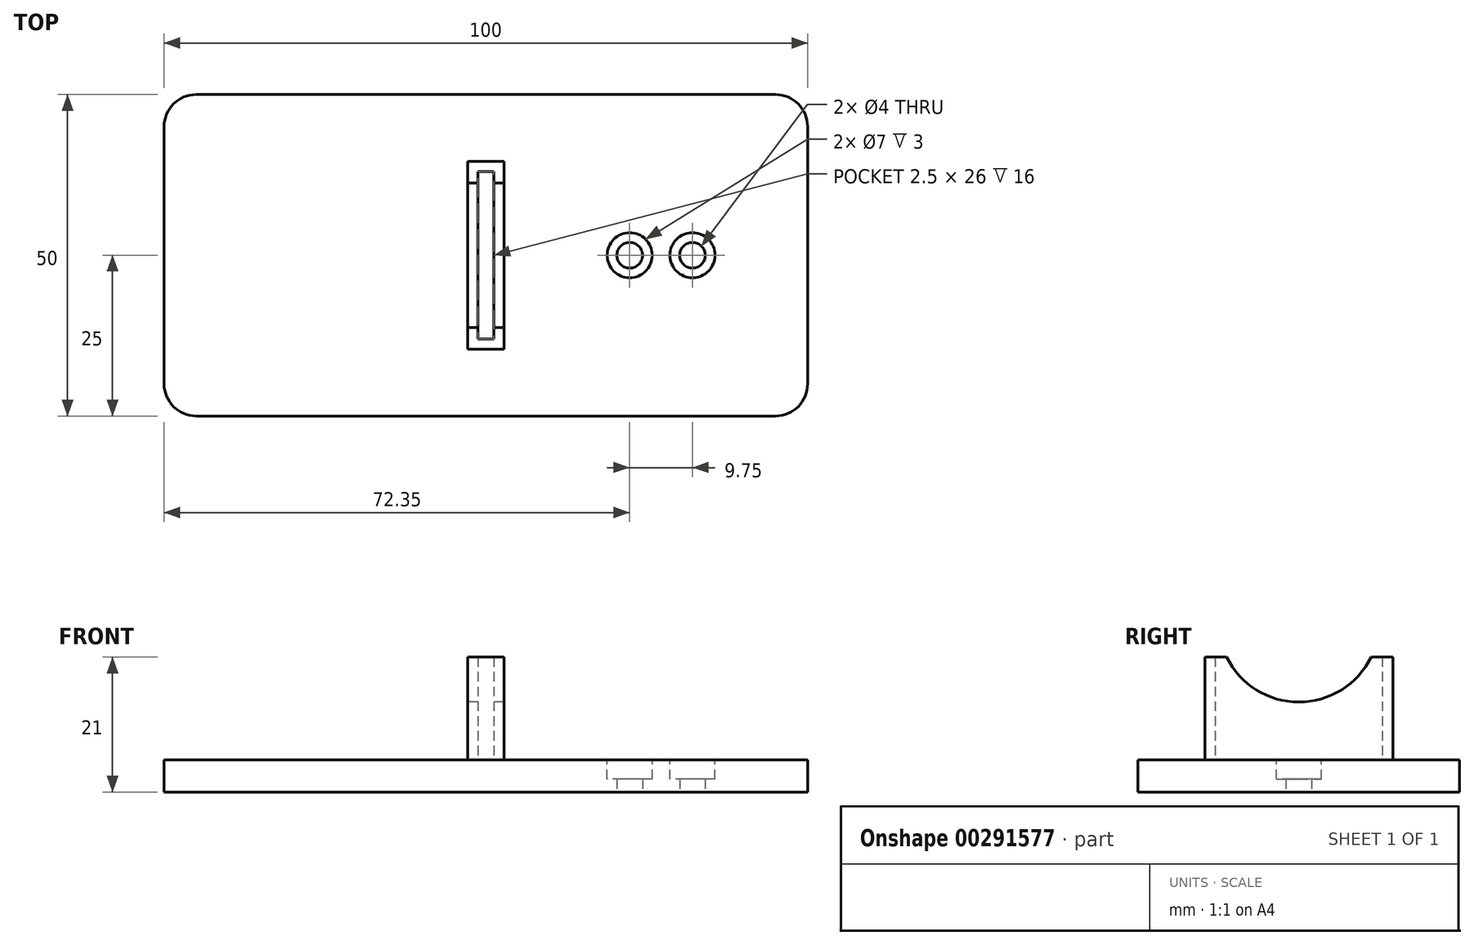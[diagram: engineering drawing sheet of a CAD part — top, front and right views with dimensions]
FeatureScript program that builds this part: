
annotation { "Feature Type Name" : "Feature", "Feature Type Description" : "" }
export const myFeature = defineFeature(function(context is Context, id is Id, definition is map)
    precondition{}
    {
        {
            var Q0;
            Q0=qCreatedBy(makeId("Top.planeOp"),FACE);
            var sketch = newSketch(context, id + "F0", { "sketchPlane" : qUnion([Q0])});
            skLineSegment(sketch, "E0.bottom", {"start": v(50, -25) * mm, "end": v(-50, -25) * mm});
            skLineSegment(sketch, "E0.top", {"start": v(50, 25) * mm, "end": v(-50, 25) * mm});
            skLineSegment(sketch, "E0.left", {"start": v(50, -25) * mm, "end": v(50, 25) * mm});
            skLineSegment(sketch, "E0.right", {"start": v(-50, -25) * mm, "end": v(-50, 25) * mm});
            skPoint(sketch, "E0.middle", {"position": v(0, 0) * mm});
            skLineSegment(sketch, "E1", {"start": v(37.6, 49.23) * mm, "end": v(37.6, -49.65) * mm, "construction": true});
            skLineSegment(sketch, "E2", {"start": v(-37.6, -45.19) * mm, "end": v(-37.6, 49.82) * mm, "construction": true});
            skCircle(sketch, "E3", {"center": v(32.1, 0) * mm, "radius": 2 * mm});
            skCircle(sketch, "E4", {"center": v(22.35, 0) * mm, "radius": 2 * mm});
            skSolve(sketch);
        }
        {
            var Q0;
            Q0=qSketchRegion(id+"F0",true);
            extrude(context, id + "F1", {"entities" : qUnion([Q0]), "depth" : 5 * mm});
        }
        {
            var Q0;
            Q0=makeQuery(id+"F1.opExtrude","CAP_FACE",FACE,{"disambiguationData":[OSD([sQuery(id+"F0.wireOp",EDGE,"E0.bottom"),sQuery(id+"F0.wireOp",EDGE,"E0.top"),sQuery(id+"F0.wireOp",EDGE,"E0.left"),sQuery(id+"F0.wireOp",EDGE,"E0.right"),sQuery(id+"F0.wireOp",EDGE,"E3"),sQuery(id+"F0.wireOp",EDGE,"E4"),sQuery(id+"F0.wireOp",EDGE,"47204b9b-54a0-4112-ab0c-eb390dbab72c0.MirrorC"),sQuery(id+"F0.wireOp",EDGE,"47204b9b-54a0-4112-ab0c-eb390dbab72c1.MirrorC")])],"isStart":false});
            var sketch = newSketch(context, id + "F2", { "sketchPlane" : qUnion([Q0])});
            skCircle(sketch, "E5.0", {"center": v(32.1, 0) * mm, "radius": 2 * mm, "construction": true});
            skCircle(sketch, "E6.0", {"center": v(22.35, 0) * mm, "radius": 2 * mm, "construction": true});
            skCircle(sketch, "E7", {"center": v(32.1, 0) * mm, "radius": 3.5 * mm});
            skCircle(sketch, "E8", {"center": v(22.35, 0) * mm, "radius": 3.5 * mm});
            skSolve(sketch);
        }
        {
            var Q0;
            Q0=qSketchRegion(id+"F2",true);
            extrude(context, id + "F3", {"entities" : qUnion([Q0]), "operationType" : NewBodyOperationType.REMOVE, "oppositeDirection" : true, "depth" : 3 * mm});
        }
        {
            var Q0;
            Q0=makeQuery(id+"F1.opExtrude","SWEPT_EDGE",EDGE,{"disambiguationData":[OSD([sQuery(id+"F0.wireOp",EDGE,"E0.bottom"),sQuery(id+"F0.wireOp",EDGE,"E0.left")])]});
            var Q1;
            Q1=makeQuery(id+"F1.opExtrude","SWEPT_EDGE",EDGE,{"disambiguationData":[OSD([sQuery(id+"F0.wireOp",EDGE,"E0.top"),sQuery(id+"F0.wireOp",EDGE,"E0.left")])]});
            var Q2;
            Q2=makeQuery(id+"F1.opExtrude","SWEPT_EDGE",EDGE,{"disambiguationData":[OSD([sQuery(id+"F0.wireOp",EDGE,"E0.bottom"),sQuery(id+"F0.wireOp",EDGE,"E0.right")])]});
            var Q3;
            Q3=makeQuery(id+"F1.opExtrude","SWEPT_EDGE",EDGE,{"disambiguationData":[OSD([sQuery(id+"F0.wireOp",EDGE,"E0.top"),sQuery(id+"F0.wireOp",EDGE,"E0.right")])]});
            fillet(context, id + "F4", {"entities" : qUnion([Q0, Q1, Q2, Q3]), "radius" : 5 * mm, "tangentPropagation" : true, "allowEdgeOverflow" : false});
        }
        {
            var Q0;
            Q0=makeQuery(id+"F1.opExtrude","CAP_FACE",FACE,{"disambiguationData":[OSD([sQuery(id+"F0.wireOp",EDGE,"E0.bottom"),sQuery(id+"F0.wireOp",EDGE,"E0.top"),sQuery(id+"F0.wireOp",EDGE,"E0.left"),sQuery(id+"F0.wireOp",EDGE,"E0.right"),sQuery(id+"F0.wireOp",EDGE,"E3"),sQuery(id+"F0.wireOp",EDGE,"E4")])],"isStart":false});
            var sketch = newSketch(context, id + "F5", { "sketchPlane" : qUnion([Q0])});
            skLineSegment(sketch, "E9.bottom", {"start": v(-1.25, 13) * mm, "end": v(1.25, 13) * mm});
            skLineSegment(sketch, "E9.top", {"start": v(-1.25, -13) * mm, "end": v(1.25, -13) * mm});
            skLineSegment(sketch, "E9.left", {"start": v(-1.25, 13) * mm, "end": v(-1.25, -13) * mm});
            skLineSegment(sketch, "E9.right", {"start": v(1.25, 13) * mm, "end": v(1.25, -13) * mm});
            skPoint(sketch, "E9.middle", {"position": v(0, 0) * mm});
            skLineSegment(sketch, "E10.bottom", {"start": v(2.85, 14.6) * mm, "end": v(-2.85, 14.6) * mm});
            skLineSegment(sketch, "E10.top", {"start": v(2.85, -14.6) * mm, "end": v(-2.85, -14.6) * mm});
            skLineSegment(sketch, "E10.left", {"start": v(2.85, 14.6) * mm, "end": v(2.85, -14.6) * mm});
            skLineSegment(sketch, "E10.right", {"start": v(-2.85, 14.6) * mm, "end": v(-2.85, -14.6) * mm});
            skSolve(sketch);
        }
        {
            var Q0;
            Q0=qSketchRegion(id+"F5",true);
            extrude(context, id + "F6", {"entities" : qUnion([Q0]), "operationType" : NewBodyOperationType.ADD, "depth" : 16 * mm});
        }
        {
            var Q0;
            Q0=makeQuery(id+"F6.opExtrude","SWEPT_FACE",FACE,{"disambiguationData":[OSD([sQuery(id+"F5.wireOp",EDGE,"E10.right")])]});
            var sketch = newSketch(context, id + "F7", { "sketchPlane" : qUnion([Q0])});
            skCircle(sketch, "E11", {"center": v(0, 26.5) * mm, "radius": 12.5 * mm});
            skLineSegment(sketch, "E12", {"start": v(26.47, 14) * mm, "end": v(-25.65, 14) * mm, "construction": true});
            skSolve(sketch);
        }
        {
            var Q0;
            Q0=qSketchRegion(id+"F7",true);
            extrude(context, id + "F8", {"entities" : qUnion([Q0]), "operationType" : NewBodyOperationType.REMOVE, "oppositeDirection" : true, "depth" : 25 * mm});
        }
    });
